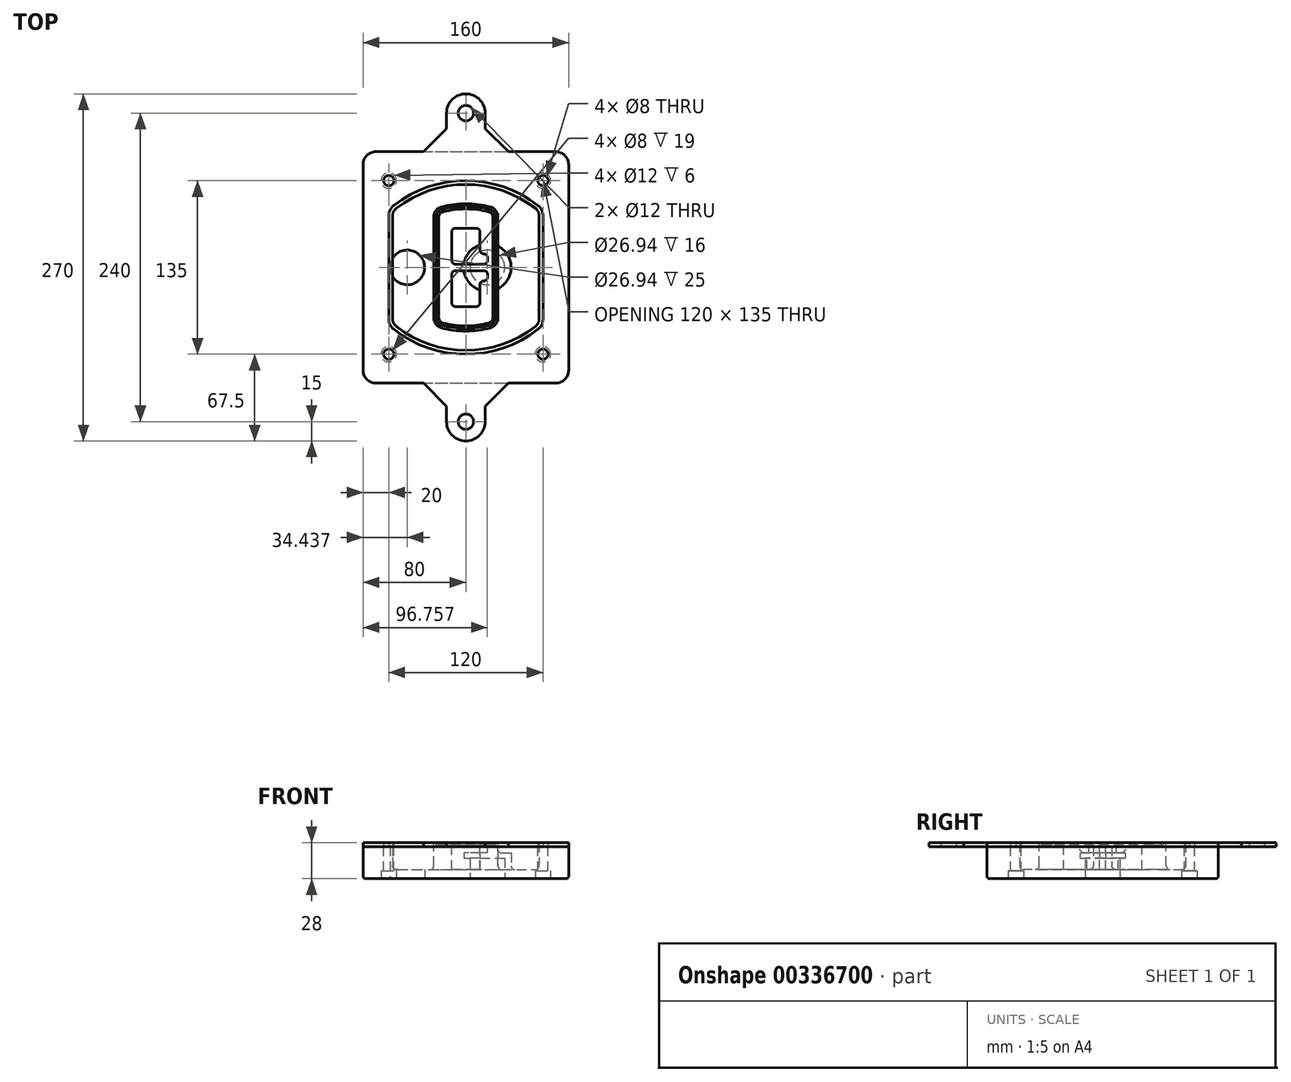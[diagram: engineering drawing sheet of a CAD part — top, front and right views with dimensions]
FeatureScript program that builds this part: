
annotation { "Feature Type Name" : "Feature", "Feature Type Description" : "" }
export const myFeature = defineFeature(function(context is Context, id is Id, definition is map)
    precondition{}
    {
        {
            var Q0;
            Q0=qCreatedBy(makeId("Top.planeOp"),FACE);
            var sketch = newSketch(context, id + "F0", { "sketchPlane" : qUnion([Q0])});
            skPoint(sketch, "E0.rect.middle", {"position": v(0, 0) * mm});
            skLineSegment(sketch, "E1.bottom", {"start": v(-70, -90) * mm, "end": v(70, -90) * mm});
            skLineSegment(sketch, "E1.top", {"start": v(-70, 90) * mm, "end": v(70, 90) * mm});
            skLineSegment(sketch, "E1.left", {"start": v(-80, -80) * mm, "end": v(-80, 80) * mm});
            skLineSegment(sketch, "E1.right", {"start": v(80, -80) * mm, "end": v(80, 80) * mm});
            skLineSegment(sketch, "E2", {"start": v(-80, 90) * mm, "end": v(80, -90) * mm, "construction": true});
            skLineSegment(sketch, "E3", {"start": v(80, 90) * mm, "end": v(-80, -90) * mm, "construction": true});
            skCircle(sketch, "E4", {"center": v(-60, 67.5) * mm, "radius": 4 * mm});
            skCircle(sketch, "E5", {"center": v(60, 67.5) * mm, "radius": 4 * mm});
            skCircle(sketch, "E6", {"center": v(60, -67.5) * mm, "radius": 4 * mm});
            skCircle(sketch, "E7", {"center": v(-60, -67.5) * mm, "radius": 4 * mm});
            skLineSegment(sketch, "E8", {"start": v(-60, 67.5) * mm, "end": v(60, 67.5) * mm, "construction": true});
            skLineSegment(sketch, "E9", {"start": v(60, 67.5) * mm, "end": v(60, -67.5) * mm, "construction": true});
            skLineSegment(sketch, "E10", {"start": v(60, -67.5) * mm, "end": v(-60, -67.5) * mm, "construction": true});
            skLineSegment(sketch, "E11", {"start": v(-60, -67.5) * mm, "end": v(-60, 67.5) * mm, "construction": true});
            skLineSegment(sketch, "E12", {"start": v(-60, 40.3) * mm, "end": v(-60, -40.3) * mm});
            skLineSegment(sketch, "E13", {"start": v(60, 40.3) * mm, "end": v(60, -40.3) * mm});
            skArc(sketch, "E14", {"start": v(56.15, 48.18) * mm, "mid": v(0, 67.5) * mm, "end": v(-56.15, 48.18) * mm});
            skArc(sketch, "E15", {"start": v(-56.15, -48.18) * mm, "mid": v(0, -67.5) * mm, "end": v(56.15, -48.18) * mm});
            skLineSegment(sketch, "E16", {"start": v(-60, 0) * mm, "end": v(60, 0) * mm, "construction": true});
            skPoint(sketch, "E17.visualSharp", {"position": v(-60, -45) * mm});
            skArc(sketch, "E17.filletArc", {"start": v(-60, -40.3) * mm, "mid": v(-58.99, -44.68) * mm, "end": v(-56.15, -48.18) * mm});
            skPoint(sketch, "E18.visualSharp", {"position": v(-60, 45) * mm});
            skArc(sketch, "E18.filletArc", {"start": v(-56.15, 48.18) * mm, "mid": v(-58.99, 44.68) * mm, "end": v(-60, 40.3) * mm});
            skPoint(sketch, "E19.visualSharp", {"position": v(60, 45) * mm});
            skArc(sketch, "E19.filletArc", {"start": v(60, 40.3) * mm, "mid": v(58.99, 44.68) * mm, "end": v(56.15, 48.18) * mm});
            skPoint(sketch, "E20.visualSharp", {"position": v(60, -45) * mm});
            skArc(sketch, "E20.filletArc", {"start": v(56.15, -48.18) * mm, "mid": v(58.99, -44.68) * mm, "end": v(60, -40.3) * mm});
            skPoint(sketch, "E21.visualSharp", {"position": v(-80, 90) * mm});
            skArc(sketch, "E21.filletArc", {"start": v(-70, 90) * mm, "mid": v(-77.07, 87.07) * mm, "end": v(-80, 80) * mm});
            skPoint(sketch, "E22.visualSharp", {"position": v(80, 90) * mm});
            skArc(sketch, "E22.filletArc", {"start": v(80, 80) * mm, "mid": v(77.07, 87.07) * mm, "end": v(70, 90) * mm});
            skPoint(sketch, "E23.visualSharp", {"position": v(80, -90) * mm});
            skArc(sketch, "E23.filletArc", {"start": v(70, -90) * mm, "mid": v(77.07, -87.07) * mm, "end": v(80, -80) * mm});
            skPoint(sketch, "E24.visualSharp", {"position": v(-80, -90) * mm});
            skArc(sketch, "E24.filletArc", {"start": v(-80, -80) * mm, "mid": v(-77.07, -87.07) * mm, "end": v(-70, -90) * mm});
            skArc(sketch, "E25.0", {"start": v(57, 40.3) * mm, "mid": v(56.3, 43.36) * mm, "end": v(54.3, 45.81) * mm});
            skLineSegment(sketch, "E25.1", {"start": v(57, 40.3) * mm, "end": v(57, -40.3) * mm});
            skArc(sketch, "E25.2", {"start": v(54.3, -45.81) * mm, "mid": v(56.3, -43.36) * mm, "end": v(57, -40.3) * mm});
            skArc(sketch, "E25.3", {"start": v(-54.3, -45.81) * mm, "mid": v(0, -64.5) * mm, "end": v(54.3, -45.81) * mm});
            skArc(sketch, "E25.4", {"start": v(-57, -40.3) * mm, "mid": v(-56.3, -43.36) * mm, "end": v(-54.3, -45.81) * mm});
            skArc(sketch, "E25.5", {"start": v(54.3, 45.81) * mm, "mid": v(0, 64.5) * mm, "end": v(-54.3, 45.81) * mm});
            skLineSegment(sketch, "E25.6", {"start": v(-57, 40.3) * mm, "end": v(-57, -40.3) * mm});
            skArc(sketch, "E25.7", {"start": v(-54.3, 45.81) * mm, "mid": v(-56.3, 43.36) * mm, "end": v(-57, 40.3) * mm});
            skArc(sketch, "E26.0", {"start": v(-58.62, 51.33) * mm, "mid": v(-62.58, 46.43) * mm, "end": v(-64, 40.3) * mm});
            skArc(sketch, "E26.1", {"start": v(58.62, 51.33) * mm, "mid": v(0, 71.5) * mm, "end": v(-58.62, 51.33) * mm});
            skArc(sketch, "E26.2", {"start": v(64, 40.3) * mm, "mid": v(62.58, 46.43) * mm, "end": v(58.62, 51.33) * mm});
            skLineSegment(sketch, "E26.3", {"start": v(64, 40.3) * mm, "end": v(64, -40.3) * mm});
            skArc(sketch, "E26.4", {"start": v(58.62, -51.33) * mm, "mid": v(62.58, -46.43) * mm, "end": v(64, -40.3) * mm});
            skLineSegment(sketch, "E26.5", {"start": v(-64, 40.3) * mm, "end": v(-64, -40.3) * mm});
            skArc(sketch, "E26.6", {"start": v(-58.62, -51.33) * mm, "mid": v(0, -71.5) * mm, "end": v(58.62, -51.33) * mm});
            skArc(sketch, "E26.7", {"start": v(-64, -40.3) * mm, "mid": v(-62.58, -46.43) * mm, "end": v(-58.62, -51.33) * mm});
            skSolve(sketch);
        }
        {
            var Q0;
            Q0=makeQuery(id+"F0.imprint","IMPRINT",FACE,{"disambiguationData":[TD([[makeQuery(id+"F0.imprint","IMPRINT",EDGE,{"derivedFrom":sQuery(id+"F0.wireOp",EDGE,"E1.bottom")}),1.0]])]});
            var Q1;
            Q1=makeQuery(id+"F0.imprint","IMPRINT",FACE,{"disambiguationData":[TD([[makeQuery(id+"F0.imprint","IMPRINT",EDGE,{"derivedFrom":sQuery(id+"F0.wireOp",EDGE,"E12")}),1.0]])]});
            var Q2;
            Q2=makeQuery(id+"F0.imprint","IMPRINT",FACE,{"disambiguationData":[TD([[makeQuery(id+"F0.imprint","IMPRINT",EDGE,{"derivedFrom":sQuery(id+"F0.wireOp",EDGE,"E25.0")}),1.0]])]});
            var Q3;
            Q3=makeQuery(id+"F0.imprint","IMPRINT",FACE,{"disambiguationData":[TD([[makeQuery(id+"F0.imprint","IMPRINT",EDGE,{"derivedFrom":sQuery(id+"F0.wireOp",EDGE,"E12")}),-1.0]])]});
            extrude(context, id + "F1", {"entities" : qUnion([Q0, Q1, Q2, Q3]), "oppositeDirection" : true, "depth" : 25 * mm});
        }
        {
            var Q0;
            Q0=makeQuery(id+"F0.imprint","IMPRINT",FACE,{"disambiguationData":[TD([[makeQuery(id+"F0.imprint","IMPRINT",EDGE,{"derivedFrom":sQuery(id+"F0.wireOp",EDGE,"E12")}),1.0]])]});
            extrude(context, id + "F2", {"entities" : qUnion([Q0]), "operationType" : NewBodyOperationType.ADD, "depth" : 3 * mm});
        }
        {
            var Q0;
            Q0=makeQuery(id+"F0.imprint","IMPRINT",FACE,{"disambiguationData":[TD([[makeQuery(id+"F0.imprint","IMPRINT",EDGE,{"derivedFrom":sQuery(id+"F0.wireOp",EDGE,"E25.0")}),1.0]])]});
            extrude(context, id + "F3", {"entities" : qUnion([Q0]), "operationType" : NewBodyOperationType.REMOVE, "oppositeDirection" : true, "depth" : 18 * mm});
        }
        {
            var Q0;
            Q0=makeQuery(id+"F2.opExtrude","CAP_FACE",FACE,{"disambiguationData":[OSD([sQuery(id+"F0.wireOp",EDGE,"E12"),sQuery(id+"F0.wireOp",EDGE,"E13"),sQuery(id+"F0.wireOp",EDGE,"E14"),sQuery(id+"F0.wireOp",EDGE,"E15"),sQuery(id+"F0.wireOp",EDGE,"E17.filletArc"),sQuery(id+"F0.wireOp",EDGE,"E18.filletArc"),sQuery(id+"F0.wireOp",EDGE,"E19.filletArc"),sQuery(id+"F0.wireOp",EDGE,"E20.filletArc"),sQuery(id+"F0.wireOp",EDGE,"E25.0"),sQuery(id+"F0.wireOp",EDGE,"E25.1"),sQuery(id+"F0.wireOp",EDGE,"E25.2"),sQuery(id+"F0.wireOp",EDGE,"E25.3"),sQuery(id+"F0.wireOp",EDGE,"E25.4"),sQuery(id+"F0.wireOp",EDGE,"E25.5"),sQuery(id+"F0.wireOp",EDGE,"E25.6"),sQuery(id+"F0.wireOp",EDGE,"E25.7")])],"isStart":false});
            var sketch = newSketch(context, id + "F4", { "sketchPlane" : qUnion([Q0])});
            skArc(sketch, "E27.0", {"start": v(-19.08, -46.97) * mm, "mid": v(0, -49.5) * mm, "end": v(19.08, -46.97) * mm});
            skArc(sketch, "E28.0", {"start": v(19.08, 46.97) * mm, "mid": v(0, 49.5) * mm, "end": v(-19.08, 46.97) * mm});
            skLineSegment(sketch, "E29", {"start": v(-25, 39.25) * mm, "end": v(-25, -39.25) * mm});
            skLineSegment(sketch, "E30", {"start": v(25, 39.25) * mm, "end": v(25, -39.25) * mm});
            skLineSegment(sketch, "E31", {"start": v(-25, 45.1) * mm, "end": v(25, 45.1) * mm, "construction": true});
            skLineSegment(sketch, "E32", {"start": v(-25, -45.1) * mm, "end": v(25, -45.1) * mm, "construction": true});
            skPoint(sketch, "E33.visualSharp", {"position": v(-25, 45.1) * mm});
            skArc(sketch, "E33.filletArc", {"start": v(-19.08, 46.97) * mm, "mid": v(-23.35, 44.11) * mm, "end": v(-25, 39.25) * mm});
            skPoint(sketch, "E34.visualSharp", {"position": v(25, 45.1) * mm});
            skArc(sketch, "E34.filletArc", {"start": v(25, 39.25) * mm, "mid": v(23.35, 44.11) * mm, "end": v(19.08, 46.97) * mm});
            skPoint(sketch, "E35.visualSharp", {"position": v(25, -45.1) * mm});
            skArc(sketch, "E35.filletArc", {"start": v(19.08, -46.97) * mm, "mid": v(23.35, -44.11) * mm, "end": v(25, -39.25) * mm});
            skPoint(sketch, "E36.visualSharp", {"position": v(-25, -45.1) * mm});
            skArc(sketch, "E36.filletArc", {"start": v(-25, -39.25) * mm, "mid": v(-23.35, -44.11) * mm, "end": v(-19.08, -46.97) * mm});
            skArc(sketch, "E37.0", {"start": v(54.3, 45.81) * mm, "mid": v(0, 64.5) * mm, "end": v(-54.3, 45.81) * mm});
            skArc(sketch, "E37.1", {"start": v(-54.3, 45.81) * mm, "mid": v(-56.3, 43.36) * mm, "end": v(-57, 40.3) * mm});
            skLineSegment(sketch, "E37.2", {"start": v(-57, 40.3) * mm, "end": v(-57, -40.3) * mm});
            skArc(sketch, "E37.3", {"start": v(-57, -40.3) * mm, "mid": v(-56.3, -43.36) * mm, "end": v(-54.3, -45.81) * mm});
            skArc(sketch, "E37.4", {"start": v(-54.3, -45.81) * mm, "mid": v(0, -64.5) * mm, "end": v(54.3, -45.81) * mm});
            skArc(sketch, "E37.5", {"start": v(54.3, -45.81) * mm, "mid": v(56.3, -43.36) * mm, "end": v(57, -40.3) * mm});
            skLineSegment(sketch, "E37.6", {"start": v(57, 40.3) * mm, "end": v(57, -40.3) * mm});
            skArc(sketch, "E37.7", {"start": v(57, 40.3) * mm, "mid": v(56.3, 43.36) * mm, "end": v(54.3, 45.81) * mm});
            skLineSegment(sketch, "E38.0", {"start": v(23, 39.25) * mm, "end": v(23, -39.25) * mm});
            skArc(sketch, "E38.1", {"start": v(18.56, -45.04) * mm, "mid": v(21.76, -42.9) * mm, "end": v(23, -39.25) * mm});
            skArc(sketch, "E38.2", {"start": v(-18.56, -45.04) * mm, "mid": v(0, -47.5) * mm, "end": v(18.56, -45.04) * mm});
            skArc(sketch, "E38.3", {"start": v(-23, -39.25) * mm, "mid": v(-21.76, -42.9) * mm, "end": v(-18.56, -45.04) * mm});
            skLineSegment(sketch, "E38.4", {"start": v(-23, 39.25) * mm, "end": v(-23, -39.25) * mm});
            skArc(sketch, "E38.5", {"start": v(23, 39.25) * mm, "mid": v(21.76, 42.9) * mm, "end": v(18.56, 45.04) * mm});
            skArc(sketch, "E38.6", {"start": v(-18.56, 45.04) * mm, "mid": v(-21.76, 42.9) * mm, "end": v(-23, 39.25) * mm});
            skArc(sketch, "E38.7", {"start": v(18.56, 45.04) * mm, "mid": v(0, 47.5) * mm, "end": v(-18.56, 45.04) * mm});
            skArc(sketch, "E39.0", {"start": v(21, 39.25) * mm, "mid": v(20.18, 41.68) * mm, "end": v(18.04, 43.1) * mm});
            skLineSegment(sketch, "E39.1", {"start": v(21, 39.25) * mm, "end": v(21, -39.25) * mm});
            skArc(sketch, "E39.2", {"start": v(18.04, -43.1) * mm, "mid": v(20.18, -41.68) * mm, "end": v(21, -39.25) * mm});
            skArc(sketch, "E39.3", {"start": v(-18.04, -43.1) * mm, "mid": v(0, -45.5) * mm, "end": v(18.04, -43.1) * mm});
            skArc(sketch, "E39.4", {"start": v(-21, -39.25) * mm, "mid": v(-20.18, -41.68) * mm, "end": v(-18.04, -43.1) * mm});
            skArc(sketch, "E39.5", {"start": v(18.04, 43.1) * mm, "mid": v(0, 45.5) * mm, "end": v(-18.04, 43.1) * mm});
            skLineSegment(sketch, "E39.6", {"start": v(-21, 39.25) * mm, "end": v(-21, -39.25) * mm});
            skArc(sketch, "E39.7", {"start": v(-18.04, 43.1) * mm, "mid": v(-20.18, 41.68) * mm, "end": v(-21, 39.25) * mm});
            skLineSegment(sketch, "E40", {"start": v(-25, 0) * mm, "end": v(25, 0) * mm, "construction": true});
            skLineSegment(sketch, "E41", {"start": v(-11, 5.5) * mm, "end": v(-11, 27.5) * mm});
            skLineSegment(sketch, "E42", {"start": v(-8, 30.5) * mm, "end": v(8, 30.5) * mm});
            skLineSegment(sketch, "E43", {"start": v(11, 27.5) * mm, "end": v(11, 13.5) * mm});
            skLineSegment(sketch, "E44", {"start": v(14, 10.5) * mm, "end": v(14, 10.5) * mm});
            skLineSegment(sketch, "E45", {"start": v(17, 7.5) * mm, "end": v(17, 5.5) * mm});
            skLineSegment(sketch, "E46", {"start": v(14, 2.5) * mm, "end": v(-8, 2.5) * mm});
            skPoint(sketch, "E47.visualSharp", {"position": v(-11, 30.5) * mm});
            skArc(sketch, "E47.filletArc", {"start": v(-8, 30.5) * mm, "mid": v(-10.12, 29.62) * mm, "end": v(-11, 27.5) * mm});
            skPoint(sketch, "E48.visualSharp", {"position": v(11, 30.5) * mm});
            skArc(sketch, "E48.filletArc", {"start": v(11, 27.5) * mm, "mid": v(10.12, 29.62) * mm, "end": v(8, 30.5) * mm});
            skPoint(sketch, "E49.visualSharp", {"position": v(11, 10.5) * mm});
            skArc(sketch, "E49.filletArc", {"start": v(11, 13.5) * mm, "mid": v(11.88, 11.38) * mm, "end": v(14, 10.5) * mm});
            skPoint(sketch, "E50.visualSharp", {"position": v(17, 10.5) * mm});
            skArc(sketch, "E50.filletArc", {"start": v(17, 7.5) * mm, "mid": v(16.12, 9.62) * mm, "end": v(14, 10.5) * mm});
            skPoint(sketch, "E51.visualSharp", {"position": v(17, 2.5) * mm});
            skArc(sketch, "E51.filletArc", {"start": v(14, 2.5) * mm, "mid": v(16.12, 3.38) * mm, "end": v(17, 5.5) * mm});
            skPoint(sketch, "E52.visualSharp", {"position": v(-11, 2.5) * mm});
            skArc(sketch, "E52.filletArc", {"start": v(-11, 5.5) * mm, "mid": v(-10.12, 3.38) * mm, "end": v(-8, 2.5) * mm});
            skLineSegment(sketch, "E53.0.MirrorCS", {"start": v(14, -2.5) * mm, "end": v(-8, -2.5) * mm});
            skArc(sketch, "E54.0.MirrorCS", {"start": v(-11, -5.5) * mm, "mid": v(-10.12, -3.38) * mm, "end": v(-8, -2.5) * mm});
            skLineSegment(sketch, "E55.0.MirrorCS", {"start": v(-11, -5.5) * mm, "end": v(-11, -27.5) * mm});
            skArc(sketch, "E56.0.MirrorCS", {"start": v(-8, -30.5) * mm, "mid": v(-10.12, -29.62) * mm, "end": v(-11, -27.5) * mm});
            skLineSegment(sketch, "E57.0.MirrorCS", {"start": v(-8, -30.5) * mm, "end": v(8, -30.5) * mm});
            skArc(sketch, "E58.0.MirrorCS", {"start": v(11, -27.5) * mm, "mid": v(10.12, -29.62) * mm, "end": v(8, -30.5) * mm});
            skLineSegment(sketch, "E59.0.MirrorCS", {"start": v(11, -27.5) * mm, "end": v(11, -13.5) * mm});
            skArc(sketch, "E60.0.MirrorCS", {"start": v(11, -13.5) * mm, "mid": v(11.88, -11.38) * mm, "end": v(14, -10.5) * mm});
            skArc(sketch, "E61.0.MirrorCS", {"start": v(17, -7.5) * mm, "mid": v(16.12, -9.62) * mm, "end": v(14, -10.5) * mm});
            skLineSegment(sketch, "E62.0.MirrorCS", {"start": v(17, -7.5) * mm, "end": v(17, -5.5) * mm});
            skArc(sketch, "E63.0.MirrorCS", {"start": v(14, -2.5) * mm, "mid": v(16.12, -3.38) * mm, "end": v(17, -5.5) * mm});
            skSolve(sketch);
        }
        {
            var Q0;
            Q0=makeQuery(id+"F4.imprint","IMPRINT",FACE,{"disambiguationData":[TD([[makeQuery(id+"F4.imprint","IMPRINT",EDGE,{"derivedFrom":sQuery(id+"F4.wireOp",EDGE,"E27.0")}),1.0]])]});
            var Q1;
            Q1=makeQuery(id+"F4.imprint","IMPRINT",FACE,{"disambiguationData":[TD([[makeQuery(id+"F4.imprint","IMPRINT",EDGE,{"derivedFrom":sQuery(id+"F4.wireOp",EDGE,"E38.0")}),-1.0]])]});
            var Q2;
            Q2=makeQuery(id+"F4.imprint","IMPRINT",FACE,{"disambiguationData":[TD([[makeQuery(id+"F4.imprint","IMPRINT",EDGE,{"derivedFrom":sQuery(id+"F4.wireOp",EDGE,"E39.0")}),1.0]])]});
            extrude(context, id + "F5", {"entities" : qUnion([Q0, Q1, Q2]), "operationType" : NewBodyOperationType.ADD, "endBound" : BoundingType.UP_TO_NEXT, "oppositeDirection" : true, "depth" : 25 * mm});
        }
        {
            var Q0;
            Q0=makeQuery(id+"F4.imprint","IMPRINT",FACE,{"disambiguationData":[TD([[makeQuery(id+"F4.imprint","IMPRINT",EDGE,{"derivedFrom":sQuery(id+"F4.wireOp",EDGE,"E38.0")}),-1.0]])]});
            extrude(context, id + "F6", {"entities" : qUnion([Q0]), "operationType" : NewBodyOperationType.REMOVE, "oppositeDirection" : true, "depth" : 2 * mm});
        }
        {
            var Q0;
            Q0=makeQuery(id+"F1.opExtrude","CAP_FACE",FACE,{"disambiguationData":[OSD([sQuery(id+"F0.wireOp",EDGE,"E1.bottom"),sQuery(id+"F0.wireOp",EDGE,"E1.top"),sQuery(id+"F0.wireOp",EDGE,"E1.left"),sQuery(id+"F0.wireOp",EDGE,"E1.right"),sQuery(id+"F0.wireOp",EDGE,"E4"),sQuery(id+"F0.wireOp",EDGE,"E5"),sQuery(id+"F0.wireOp",EDGE,"E6"),sQuery(id+"F0.wireOp",EDGE,"E7"),sQuery(id+"F0.wireOp",EDGE,"E21.filletArc"),sQuery(id+"F0.wireOp",EDGE,"E22.filletArc"),sQuery(id+"F0.wireOp",EDGE,"E23.filletArc"),sQuery(id+"F0.wireOp",EDGE,"E24.filletArc")])],"isStart":false});
            var sketch = newSketch(context, id + "F7", { "sketchPlane" : qUnion([Q0])});
            skCircle(sketch, "E64", {"center": v(16.76, 0) * mm, "radius": 13.47 * mm});
            skCircle(sketch, "E65", {"center": v(-45.56, 0) * mm, "radius": 13.47 * mm});
            skLineSegment(sketch, "E66", {"start": v(80, 0) * mm, "end": v(-80, 0) * mm});
            skCircle(sketch, "E67", {"center": v(16.76, 0) * mm, "radius": 18.47 * mm});
            skCircle(sketch, "E68", {"center": v(60, -67.5) * mm, "radius": 6 * mm});
            skCircle(sketch, "E69", {"center": v(-60, -67.5) * mm, "radius": 6 * mm});
            skCircle(sketch, "E70", {"center": v(-60, 67.5) * mm, "radius": 6 * mm});
            skCircle(sketch, "E71", {"center": v(60, 67.5) * mm, "radius": 6 * mm});
            skSolve(sketch);
        }
        {
            var Q0;
            {var subQ1=sQuery(id+"F7.wireOp",EDGE,"E66");var subQ4=sQuery(id+"F7.wireOp",EDGE,"E64");var subQ6=makeQuery(id+"F7.imprint","INTERSECT",VERTEX,{"disambiguationData":[OD(0.0)],"derivedFrom":[subQ4,subQ1]});Q0=makeQuery(id+"F7.imprint","IMPRINT",FACE,{"disambiguationData":[TD([[makeQuery(id+"F7.imprint","IMPRINT",EDGE,{"disambiguationData":[TD([[subQ6,-1.0]])],"derivedFrom":subQ4}),-1.0]])]});}
            var Q1;
            {var subQ0=sQuery(id+"F7.wireOp",EDGE,"E66");var subQ1=sQuery(id+"F7.wireOp",EDGE,"E64");var subQ3=makeQuery(id+"F7.imprint","INTERSECT",VERTEX,{"disambiguationData":[OD(0.0)],"derivedFrom":[subQ1,subQ0]});Q1=makeQuery(id+"F7.imprint","IMPRINT",FACE,{"disambiguationData":[TD([[makeQuery(id+"F7.imprint","IMPRINT",EDGE,{"disambiguationData":[TD([[subQ3,-1.0]])],"derivedFrom":subQ1}),1.0]])]});}
            var Q2;
            {var subQ0=sQuery(id+"F7.wireOp",EDGE,"E66");var subQ1=sQuery(id+"F7.wireOp",EDGE,"E64");var subQ3=makeQuery(id+"F7.imprint","INTERSECT",VERTEX,{"disambiguationData":[OD(0.0)],"derivedFrom":[subQ1,subQ0]});Q2=makeQuery(id+"F7.imprint","IMPRINT",FACE,{"disambiguationData":[TD([[makeQuery(id+"F7.imprint","IMPRINT",EDGE,{"disambiguationData":[TD([[subQ3,1.0]])],"derivedFrom":subQ1}),1.0]])]});}
            var Q3;
            {var subQ1=sQuery(id+"F7.wireOp",EDGE,"E66");var subQ4=sQuery(id+"F7.wireOp",EDGE,"E64");var subQ6=makeQuery(id+"F7.imprint","INTERSECT",VERTEX,{"disambiguationData":[OD(0.0)],"derivedFrom":[subQ4,subQ1]});Q3=makeQuery(id+"F7.imprint","IMPRINT",FACE,{"disambiguationData":[TD([[makeQuery(id+"F7.imprint","IMPRINT",EDGE,{"disambiguationData":[TD([[subQ6,1.0]])],"derivedFrom":subQ4}),-1.0]])]});}
            extrude(context, id + "F8", {"entities" : qUnion([Q0, Q1, Q2, Q3]), "operationType" : NewBodyOperationType.ADD, "oppositeDirection" : true, "depth" : 20 * mm});
        }
        {
            var Q0;
            {var subQ0=sQuery(id+"F7.wireOp",EDGE,"E66");var subQ1=sQuery(id+"F7.wireOp",EDGE,"E64");var subQ3=makeQuery(id+"F7.imprint","INTERSECT",VERTEX,{"disambiguationData":[OD(0.0)],"derivedFrom":[subQ1,subQ0]});Q0=makeQuery(id+"F7.imprint","IMPRINT",FACE,{"disambiguationData":[TD([[makeQuery(id+"F7.imprint","IMPRINT",EDGE,{"disambiguationData":[TD([[subQ3,-1.0]])],"derivedFrom":subQ1}),1.0]])]});}
            var Q1;
            {var subQ0=sQuery(id+"F7.wireOp",EDGE,"E66");var subQ1=sQuery(id+"F7.wireOp",EDGE,"E64");var subQ3=makeQuery(id+"F7.imprint","INTERSECT",VERTEX,{"disambiguationData":[OD(0.0)],"derivedFrom":[subQ1,subQ0]});Q1=makeQuery(id+"F7.imprint","IMPRINT",FACE,{"disambiguationData":[TD([[makeQuery(id+"F7.imprint","IMPRINT",EDGE,{"disambiguationData":[TD([[subQ3,1.0]])],"derivedFrom":subQ1}),1.0]])]});}
            extrude(context, id + "F9", {"entities" : qUnion([Q0, Q1]), "operationType" : NewBodyOperationType.REMOVE, "oppositeDirection" : true, "depth" : 16 * mm});
        }
        {
            var Q0;
            {var subQ0=sQuery(id+"F7.wireOp",EDGE,"E66");var subQ1=sQuery(id+"F7.wireOp",EDGE,"E65");var subQ3=makeQuery(id+"F7.imprint","INTERSECT",VERTEX,{"disambiguationData":[OD(0.0)],"derivedFrom":[subQ1,subQ0]});Q0=makeQuery(id+"F7.imprint","IMPRINT",FACE,{"disambiguationData":[TD([[makeQuery(id+"F7.imprint","IMPRINT",EDGE,{"disambiguationData":[TD([[subQ3,-1.0]])],"derivedFrom":subQ1}),1.0]])]});}
            var Q1;
            {var subQ0=sQuery(id+"F7.wireOp",EDGE,"E66");var subQ1=sQuery(id+"F7.wireOp",EDGE,"E65");var subQ3=makeQuery(id+"F7.imprint","INTERSECT",VERTEX,{"disambiguationData":[OD(0.0)],"derivedFrom":[subQ1,subQ0]});Q1=makeQuery(id+"F7.imprint","IMPRINT",FACE,{"disambiguationData":[TD([[makeQuery(id+"F7.imprint","IMPRINT",EDGE,{"disambiguationData":[TD([[subQ3,1.0]])],"derivedFrom":subQ1}),1.0]])]});}
            extrude(context, id + "F10", {"entities" : qUnion([Q0, Q1]), "operationType" : NewBodyOperationType.REMOVE, "oppositeDirection" : true, "depth" : 25 * mm});
        }
        {
            var Q0;
            Q0=makeQuery(id+"F7.imprint","IMPRINT",FACE,{"disambiguationData":[TD([[makeQuery(id+"F7.imprint","IMPRINT",EDGE,{"derivedFrom":sQuery(id+"F7.wireOp",EDGE,"E68")}),1.0]])]});
            var Q1;
            Q1=makeQuery(id+"F7.imprint","IMPRINT",FACE,{"disambiguationData":[TD([[makeQuery(id+"F7.imprint","IMPRINT",EDGE,{"derivedFrom":makeQuery(id+"F1.opExtrude","CAP_EDGE",EDGE,{"disambiguationData":[OSD([sQuery(id+"F0.wireOp",EDGE,"E5")])],"isStart":false})}),-1.0]])]});
            var Q2;
            Q2=makeQuery(id+"F7.imprint","IMPRINT",FACE,{"disambiguationData":[TD([[makeQuery(id+"F7.imprint","IMPRINT",EDGE,{"derivedFrom":sQuery(id+"F7.wireOp",EDGE,"E69")}),1.0]])]});
            var Q3;
            Q3=makeQuery(id+"F7.imprint","IMPRINT",FACE,{"disambiguationData":[TD([[makeQuery(id+"F7.imprint","IMPRINT",EDGE,{"derivedFrom":makeQuery(id+"F1.opExtrude","CAP_EDGE",EDGE,{"disambiguationData":[OSD([sQuery(id+"F0.wireOp",EDGE,"E4")])],"isStart":false})}),-1.0]])]});
            var Q4;
            Q4=makeQuery(id+"F7.imprint","IMPRINT",FACE,{"disambiguationData":[TD([[makeQuery(id+"F7.imprint","IMPRINT",EDGE,{"derivedFrom":sQuery(id+"F7.wireOp",EDGE,"E70")}),1.0]])]});
            var Q5;
            Q5=makeQuery(id+"F7.imprint","IMPRINT",FACE,{"disambiguationData":[TD([[makeQuery(id+"F7.imprint","IMPRINT",EDGE,{"derivedFrom":makeQuery(id+"F1.opExtrude","CAP_EDGE",EDGE,{"disambiguationData":[OSD([sQuery(id+"F0.wireOp",EDGE,"E7")])],"isStart":false})}),-1.0]])]});
            var Q6;
            Q6=makeQuery(id+"F7.imprint","IMPRINT",FACE,{"disambiguationData":[TD([[makeQuery(id+"F7.imprint","IMPRINT",EDGE,{"derivedFrom":sQuery(id+"F7.wireOp",EDGE,"E71")}),1.0]])]});
            var Q7;
            Q7=makeQuery(id+"F7.imprint","IMPRINT",FACE,{"disambiguationData":[TD([[makeQuery(id+"F7.imprint","IMPRINT",EDGE,{"derivedFrom":makeQuery(id+"F1.opExtrude","CAP_EDGE",EDGE,{"disambiguationData":[OSD([sQuery(id+"F0.wireOp",EDGE,"E6")])],"isStart":false})}),-1.0]])]});
            extrude(context, id + "F11", {"entities" : qUnion([Q0, Q1, Q2, Q3, Q4, Q5, Q6, Q7]), "operationType" : NewBodyOperationType.REMOVE, "oppositeDirection" : true, "depth" : 6 * mm});
        }
        {
            var Q0;
            Q0=makeQuery(id+"F9.boolean.opBoolean","COPY",FACE,{"derivedFrom":makeQuery(id+"F9.opExtrude","CAP_FACE",FACE,{"disambiguationData":[OSD([sQuery(id+"F7.wireOp",EDGE,"E64")])],"isStart":false})});
            var sketch = newSketch(context, id + "F12", { "sketchPlane" : qUnion([Q0])});
            skArc(sketch, "E72.0", {"start": v(11, 17.55) * mm, "mid": v(2.57, 11.82) * mm, "end": v(-1.54, 2.5) * mm});
            skArc(sketch, "E72.1", {"start": v(-1.54, -2.5) * mm, "mid": v(2.57, -11.82) * mm, "end": v(11, -17.55) * mm});
            skLineSegment(sketch, "E73", {"start": v(-1.54, -2.5) * mm, "end": v(14, -2.5) * mm});
            skLineSegment(sketch, "E74.0", {"start": v(14, 2.5) * mm, "end": v(-1.54, 2.5) * mm});
            skArc(sketch, "E74.1", {"start": v(14, 2.5) * mm, "mid": v(16.12, 3.38) * mm, "end": v(17, 5.5) * mm});
            skLineSegment(sketch, "E74.2", {"start": v(17, 7.5) * mm, "end": v(17, 5.5) * mm});
            skArc(sketch, "E74.3", {"start": v(17, 7.5) * mm, "mid": v(16.12, 9.62) * mm, "end": v(14, 10.5) * mm});
            skArc(sketch, "E74.4", {"start": v(11, 13.5) * mm, "mid": v(11.88, 11.38) * mm, "end": v(14, 10.5) * mm});
            skLineSegment(sketch, "E74.5", {"start": v(11, 17.55) * mm, "end": v(11, 13.5) * mm});
            skLineSegment(sketch, "E74.7", {"start": v(14, -2.5) * mm, "end": v(-1.54, -2.5) * mm});
            skArc(sketch, "E74.8", {"start": v(14, -2.5) * mm, "mid": v(16.12, -3.38) * mm, "end": v(17, -5.5) * mm});
            skLineSegment(sketch, "E74.9", {"start": v(17, -7.5) * mm, "end": v(17, -5.5) * mm});
            skArc(sketch, "E74.10", {"start": v(17, -7.5) * mm, "mid": v(16.12, -9.62) * mm, "end": v(14, -10.5) * mm});
            skArc(sketch, "E74.11", {"start": v(11, -13.5) * mm, "mid": v(11.88, -11.38) * mm, "end": v(14, -10.5) * mm});
            skLineSegment(sketch, "E74.12", {"start": v(11, -17.55) * mm, "end": v(11, -13.5) * mm});
            skPoint(sketch, "E75.orphan", {"position": v(11, -27.5) * mm});
            skPoint(sketch, "E76.orphan", {"position": v(-8, -2.5) * mm});
            skPoint(sketch, "E77.orphan", {"position": v(-8, 2.5) * mm});
            skPoint(sketch, "E78.orphan", {"position": v(11, 27.5) * mm});
            skSolve(sketch);
        }
        {
            var Q0;
            {var subQ7=sQuery(id+"F12.wireOp",EDGE,"E72.0");var subQ14=sQuery(id+"F12.wireOp",EDGE,"E72.1");var subQ16=sQuery(id+"F12.wireOp",EDGE,"E74.1");var subQ18=sQuery(id+"F12.wireOp",EDGE,"E74.8");Q0=qUnion([makeQuery(id+"F12.imprint","IMPRINT",FACE,{"disambiguationData":[TD([[makeQuery(id+"F12.imprint","IMPRINT",EDGE,{"derivedFrom":subQ7}),1.0]])]}),makeQuery(id+"F12.imprint","IMPRINT",FACE,{"disambiguationData":[TD([[makeQuery(id+"F12.imprint","IMPRINT",EDGE,{"derivedFrom":subQ14}),1.0]])]}),makeQuery(id+"F12.imprint","IMPRINT",FACE,{"disambiguationData":[TD([[makeQuery(id+"F12.imprint","IMPRINT",EDGE,{"derivedFrom":subQ16}),1.0]])]}),makeQuery(id+"F12.imprint","IMPRINT",FACE,{"disambiguationData":[TD([[makeQuery(id+"F12.imprint","IMPRINT",EDGE,{"derivedFrom":subQ18}),-1.0]])]})]);}
            var Q1;
            Q1=makeQuery(id+"F5.boolean.opBoolean","SPLIT",FACE,{"disambiguationData":[TD([makeQuery(id+"F5.opExtrude","SWEPT_FACE",FACE,{"disambiguationData":[OSD([sQuery(id+"F4.wireOp",EDGE,"E41")])]})])],"derivedFrom":makeQuery(id+"F3.boolean.opBoolean","COPY",FACE,{"derivedFrom":makeQuery(id+"F3.opExtrude","CAP_FACE",FACE,{"disambiguationData":[OSD([sQuery(id+"F0.wireOp",EDGE,"E25.0"),sQuery(id+"F0.wireOp",EDGE,"E25.1"),sQuery(id+"F0.wireOp",EDGE,"E25.2"),sQuery(id+"F0.wireOp",EDGE,"E25.3"),sQuery(id+"F0.wireOp",EDGE,"E25.4"),sQuery(id+"F0.wireOp",EDGE,"E25.5"),sQuery(id+"F0.wireOp",EDGE,"E25.6"),sQuery(id+"F0.wireOp",EDGE,"E25.7")])],"isStart":false})})});
            extrude(context, id + "F13", {"entities" : qUnion([Q0]), "operationType" : NewBodyOperationType.REMOVE, "endBound" : BoundingType.UP_TO_SURFACE, "endBoundEntityFace" : qUnion([Q1]), "depth" : 25 * mm});
        }
        {
            var Q0;
            Q0=makeQuery(id+"F3.boolean.opBoolean","COPY",EDGE,{"derivedFrom":makeQuery(id+"F3.opExtrude","CAP_EDGE",EDGE,{"disambiguationData":[OSD([sQuery(id+"F0.wireOp",EDGE,"E25.6")])],"isStart":false})});
            var Q1;
            Q1=makeQuery(id+"F8.boolean.opBoolean","INTERSECT",EDGE,{"derivedFrom":[makeQuery(id+"F5.opExtrude","SWEPT_FACE",FACE,{"disambiguationData":[OSD([sQuery(id+"F4.wireOp",EDGE,"E30")])]}),makeQuery(id+"F8.opExtrude","CAP_FACE",FACE,{"disambiguationData":[OSD([sQuery(id+"F7.wireOp",EDGE,"E67")])],"isStart":false})]});
            var Q2;
            Q2=makeQuery(id+"F8.boolean.opBoolean","INTERSECT",EDGE,{"disambiguationData":[OD(1.0)],"derivedFrom":[makeQuery(id+"F5.opExtrude","SWEPT_FACE",FACE,{"disambiguationData":[OSD([sQuery(id+"F4.wireOp",EDGE,"E30")])]}),makeQuery(id+"F8.opExtrude","SWEPT_FACE",FACE,{"disambiguationData":[OSD([sQuery(id+"F7.wireOp",EDGE,"E67")])]})]});
            var Q3;
            {var subQ0=sQuery(id+"F4.wireOp",EDGE,"E30");Q3=makeQuery(id+"F8.boolean.opBoolean","SPLIT",EDGE,{"disambiguationData":[TD([makeQuery(id+"F5.opExtrude","SWEPT_FACE",FACE,{"disambiguationData":[OSD([sQuery(id+"F4.wireOp",EDGE,"E35.filletArc")])]})])],"derivedFrom":makeQuery(id+"F5.opExtrude","CAP_EDGE",EDGE,{"disambiguationData":[OSD([subQ0])],"isStart":false})});}
            var Q4;
            {var subQ0=sQuery(id+"F0.wireOp",EDGE,"E25.7");var subQ1=sQuery(id+"F0.wireOp",EDGE,"E25.1");var subQ2=sQuery(id+"F0.wireOp",EDGE,"E25.6");var subQ3=sQuery(id+"F0.wireOp",EDGE,"E25.5");var subQ4=sQuery(id+"F0.wireOp",EDGE,"E25.4");var subQ5=sQuery(id+"F0.wireOp",EDGE,"E25.0");var subQ6=sQuery(id+"F0.wireOp",EDGE,"E25.2");var subQ7=sQuery(id+"F0.wireOp",EDGE,"E25.3");Q4=makeQuery(id+"F8.boolean.opBoolean","INTERSECT",EDGE,{"derivedFrom":[makeQuery(id+"F5.boolean.opBoolean","SPLIT",FACE,{"disambiguationData":[TD([makeQuery(id+"F2.opExtrude","SWEPT_FACE",FACE,{"disambiguationData":[OSD([subQ5])]})])],"derivedFrom":makeQuery(id+"F3.boolean.opBoolean","COPY",FACE,{"derivedFrom":makeQuery(id+"F3.opExtrude","CAP_FACE",FACE,{"disambiguationData":[OSD([subQ5,subQ1,subQ6,subQ7,subQ4,subQ3,subQ2,subQ0])],"isStart":false})})}),makeQuery(id+"F8.opExtrude","SWEPT_FACE",FACE,{"disambiguationData":[OSD([sQuery(id+"F7.wireOp",EDGE,"E67")])]})]});}
            var Q5;
            Q5=makeQuery(id+"F8.boolean.opBoolean","INTERSECT",EDGE,{"disambiguationData":[OD(0.0)],"derivedFrom":[makeQuery(id+"F5.opExtrude","SWEPT_FACE",FACE,{"disambiguationData":[OSD([sQuery(id+"F4.wireOp",EDGE,"E30")])]}),makeQuery(id+"F8.opExtrude","SWEPT_FACE",FACE,{"disambiguationData":[OSD([sQuery(id+"F7.wireOp",EDGE,"E67")])]})]});
            fillet(context, id + "F14", {"entities" : qUnion([Q0, Q1, Q2, Q3, Q4, Q5]), "radius" : 3 * mm, "tangentPropagation" : true, "allowEdgeOverflow" : false});
        }
        {
            var Q0;
            Q0=makeQuery(id+"F1.opExtrude","CAP_EDGE",EDGE,{"disambiguationData":[OSD([sQuery(id+"F0.wireOp",EDGE,"E1.bottom")])],"isStart":false});
            fillet(context, id + "F15", {"entities" : qUnion([Q0]), "radius" : 2 * mm, "tangentPropagation" : true, "allowEdgeOverflow" : false});
        }
        {
            var Q0;
            {var subQ0=sQuery(id+"F0.wireOp",EDGE,"E21.filletArc");var subQ1=sQuery(id+"F0.wireOp",EDGE,"E7");var subQ2=sQuery(id+"F0.wireOp",EDGE,"E6");var subQ3=sQuery(id+"F0.wireOp",EDGE,"E5");var subQ4=sQuery(id+"F0.wireOp",EDGE,"E4");var subQ5=sQuery(id+"F0.wireOp",EDGE,"E22.filletArc");var subQ6=sQuery(id+"F0.wireOp",EDGE,"E1.bottom");var subQ7=sQuery(id+"F0.wireOp",EDGE,"E1.right");var subQ8=sQuery(id+"F0.wireOp",EDGE,"E1.top");var subQ9=sQuery(id+"F0.wireOp",EDGE,"E1.left");var subQ10=sQuery(id+"F0.wireOp",EDGE,"E23.filletArc");var subQ11=sQuery(id+"F0.wireOp",EDGE,"E24.filletArc");Q0=makeQuery(id+"F2.boolean.opBoolean","SPLIT",FACE,{"disambiguationData":[TD([makeQuery(id+"F1.opExtrude","SWEPT_FACE",FACE,{"disambiguationData":[OSD([subQ6])]})])],"derivedFrom":makeQuery(id+"F1.opExtrude","CAP_FACE",FACE,{"disambiguationData":[OSD([subQ6,subQ8,subQ9,subQ7,subQ4,subQ3,subQ2,subQ1,subQ0,subQ5,subQ10,subQ11])],"isStart":true})});}
            var sketch = newSketch(context, id + "F16", { "sketchPlane" : qUnion([Q0])});
            skLineSegment(sketch, "E79", {"start": v(0, 90) * mm, "end": v(0, 120) * mm, "construction": true});
            skCircle(sketch, "E80", {"center": v(0, 120) * mm, "radius": 6 * mm});
            skLineSegment(sketch, "E81", {"start": v(33, 90) * mm, "end": v(15, 108) * mm});
            skLineSegment(sketch, "E82", {"start": v(-33, 90) * mm, "end": v(-15, 108) * mm});
            skLineSegment(sketch, "E83", {"start": v(-15, 108) * mm, "end": v(-15, 120) * mm});
            skLineSegment(sketch, "E84", {"start": v(15, 108) * mm, "end": v(15, 120) * mm});
            skArc(sketch, "E85", {"start": v(15, 120) * mm, "mid": v(0, 135) * mm, "end": v(-15, 120) * mm});
            skLineSegment(sketch, "E86", {"start": v(-80, 0) * mm, "end": v(80, 0) * mm, "construction": true});
            skLineSegment(sketch, "E87.MirrorCS", {"start": v(33, -90) * mm, "end": v(15, -108) * mm});
            skLineSegment(sketch, "E88.MirrorCS", {"start": v(0, -90) * mm, "end": v(0, -120) * mm, "construction": true});
            skCircle(sketch, "E89.MirrorC", {"center": v(0, -120) * mm, "radius": 6 * mm});
            skArc(sketch, "E90.MirrorCS", {"start": v(15, -120) * mm, "mid": v(0, -135) * mm, "end": v(-15, -120) * mm});
            skLineSegment(sketch, "E91.MirrorCS", {"start": v(15, -108) * mm, "end": v(15, -120) * mm});
            skLineSegment(sketch, "E92.MirrorCS", {"start": v(-15, -108) * mm, "end": v(-15, -120) * mm});
            skLineSegment(sketch, "E93.MirrorCS", {"start": v(-33, -90) * mm, "end": v(-15, -108) * mm});
            skSolve(sketch);
        }
        {
            var Q0;
            Q0=makeQuery(id+"F16.imprint","IMPRINT",FACE,{"disambiguationData":[TD([[makeQuery(id+"F16.imprint","IMPRINT",EDGE,{"derivedFrom":sQuery(id+"F16.wireOp",EDGE,"E80")}),-1.0]])]});
            var Q1;
            Q1=makeQuery(id+"F16.imprint","IMPRINT",FACE,{"disambiguationData":[TD([[makeQuery(id+"F16.imprint","IMPRINT",EDGE,{"derivedFrom":makeQuery(id+"F1.opExtrude","CAP_EDGE",EDGE,{"disambiguationData":[OSD([sQuery(id+"F0.wireOp",EDGE,"E1.left")])],"isStart":true})}),-1.0]])]});
            var Q2;
            {var subQ0=sQuery(id+"F16.wireOp",EDGE,"E87.MirrorCS");Q2=makeQuery(id+"F16.imprint","IMPRINT",FACE,{"disambiguationData":[TD([[makeQuery(id+"F16.imprint","IMPRINT",EDGE,{"derivedFrom":subQ0}),-1.0]])]});}
            var Q3;
            Q3=makeQuery(id+"F2.opExtrude","CAP_FACE",FACE,{"disambiguationData":[OSD([sQuery(id+"F0.wireOp",EDGE,"E12"),sQuery(id+"F0.wireOp",EDGE,"E13"),sQuery(id+"F0.wireOp",EDGE,"E14"),sQuery(id+"F0.wireOp",EDGE,"E15"),sQuery(id+"F0.wireOp",EDGE,"E17.filletArc"),sQuery(id+"F0.wireOp",EDGE,"E18.filletArc"),sQuery(id+"F0.wireOp",EDGE,"E19.filletArc"),sQuery(id+"F0.wireOp",EDGE,"E20.filletArc"),sQuery(id+"F0.wireOp",EDGE,"E25.0"),sQuery(id+"F0.wireOp",EDGE,"E25.1"),sQuery(id+"F0.wireOp",EDGE,"E25.2"),sQuery(id+"F0.wireOp",EDGE,"E25.3"),sQuery(id+"F0.wireOp",EDGE,"E25.4"),sQuery(id+"F0.wireOp",EDGE,"E25.5"),sQuery(id+"F0.wireOp",EDGE,"E25.6"),sQuery(id+"F0.wireOp",EDGE,"E25.7")])],"isStart":false});
            extrude(context, id + "F17", {"entities" : qUnion([Q0, Q1, Q2]), "endBound" : BoundingType.UP_TO_SURFACE, "endBoundEntityFace" : qUnion([Q3]), "depth" : 25 * mm});
        }
    });
